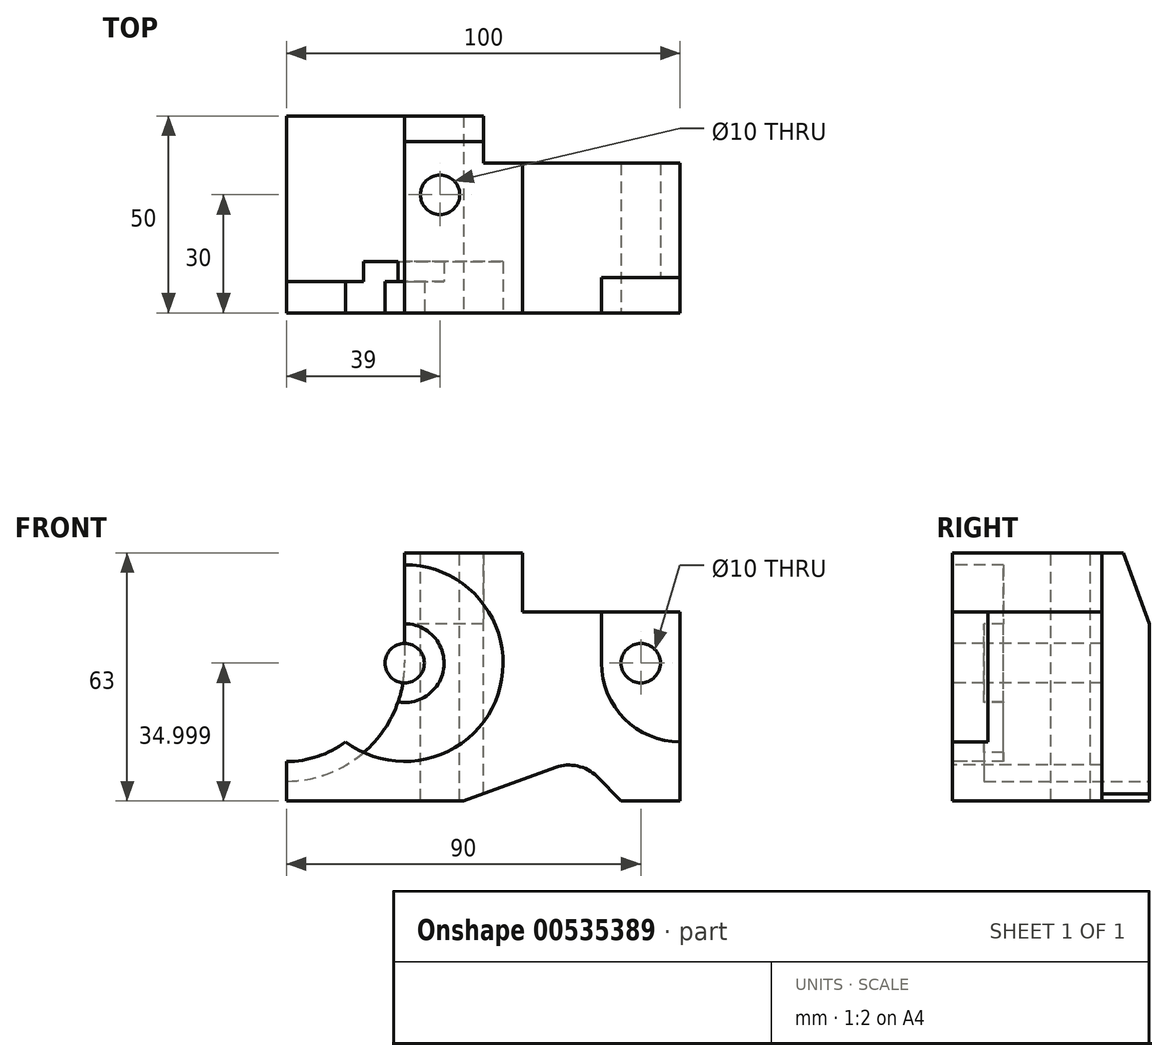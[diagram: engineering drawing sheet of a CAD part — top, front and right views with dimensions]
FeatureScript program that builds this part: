
annotation { "Feature Type Name" : "Feature", "Feature Type Description" : "" }
export const myFeature = defineFeature(function(context is Context, id is Id, definition is map)
    precondition{}
    {
        {
            var Q0;
            Q0=qCreatedBy(makeId("Front.planeOp"),FACE);
            var sketch = newSketch(context, id + "F0", { "sketchPlane" : qUnion([Q0])});
            skLineSegment(sketch, "E0.bottom", {"start": v(-90, 41.77) * mm, "end": v(-30, 41.77) * mm});
            skLineSegment(sketch, "E0.top", {"start": v(-90, -21.23) * mm, "end": v(-45, -21.23) * mm});
            skLineSegment(sketch, "E0.left", {"start": v(-90, 41.77) * mm, "end": v(-90, 38.77) * mm});
            skLineSegment(sketch, "E0.right", {"start": v(10, 26.77) * mm, "end": v(10, -21.23) * mm});
            skLineSegment(sketch, "E1", {"start": v(-45, -21.23) * mm, "end": v(-21.66, -12.74) * mm});
            skLineSegment(sketch, "E2", {"start": v(-11.17, -15.06) * mm, "end": v(-5, -21.23) * mm});
            skPoint(sketch, "E3.visualSharp", {"position": v(-15.67, -10.56) * mm});
            skArc(sketch, "E3.filletArc", {"start": v(-11.17, -15.06) * mm, "mid": v(-16.08, -12.37) * mm, "end": v(-21.66, -12.74) * mm});
            skLineSegment(sketch, "E4.trimOffspring", {"start": v(-5, -21.23) * mm, "end": v(10, -21.23) * mm});
            skLineSegment(sketch, "E5.top", {"start": v(-30, 26.77) * mm, "end": v(10, 26.77) * mm});
            skLineSegment(sketch, "E5.left", {"start": v(-30, 41.77) * mm, "end": v(-30, 26.77) * mm});
            skCircle(sketch, "E6", {"center": v(0, 13.77) * mm, "radius": 5 * mm});
            skArc(sketch, "E7", {"start": v(-90, -11.23) * mm, "mid": v(-65, 13.77) * mm, "end": v(-90, 38.77) * mm});
            skLineSegment(sketch, "E8", {"start": v(-65, 13.47) * mm, "end": v(-65, 14.07) * mm});
            skLineSegment(sketch, "E9.trimOffspring", {"start": v(-90, -11.23) * mm, "end": v(-90, -21.23) * mm});
            skSolve(sketch);
        }
        {
            var Q0;
            Q0 = qSketchRegion(id + "F0", true);
            extrude(context, id + "F1", {"entities" : qUnion([Q0]), "oppositeDirection" : true, "depth" : 50 * mm, "offsetDistance" : 25 * mm});
        }
        {
            var Q0;
            Q0=makeQuery(id+"F1.opExtrude","CAP_FACE",FACE,{"disambiguationData":[OSD([sQuery(id+"F0.wireOp",EDGE,"E0.bottom"),sQuery(id+"F0.wireOp",EDGE,"E0.top"),sQuery(id+"F0.wireOp",EDGE,"E0.left"),sQuery(id+"F0.wireOp",EDGE,"E0.right"),sQuery(id+"F0.wireOp",EDGE,"E1"),sQuery(id+"F0.wireOp",EDGE,"E2"),sQuery(id+"F0.wireOp",EDGE,"E3.filletArc"),sQuery(id+"F0.wireOp",EDGE,"E4.trimOffspring"),sQuery(id+"F0.wireOp",EDGE,"E5.top"),sQuery(id+"F0.wireOp",EDGE,"E5.left"),sQuery(id+"F0.wireOp",EDGE,"E6"),sQuery(id+"F0.wireOp",EDGE,"E7"),sQuery(id+"F0.wireOp",EDGE,"E8"),sQuery(id+"F0.wireOp",EDGE,"E9.trimOffspring")])],"isStart":false});
            var sketch = newSketch(context, id + "F2", { "sketchPlane" : qUnion([Q0])});
            skArc(sketch, "E10", {"start": v(60, 13.77) * mm, "mid": v(111.21, -7.44) * mm, "end": v(90, 43.77) * mm});
            skLineSegment(sketch, "E11", {"start": v(60, 43.77) * mm, "end": v(60, 13.77) * mm});
            skLineSegment(sketch, "E12", {"start": v(60, 43.77) * mm, "end": v(90, 43.77) * mm});
            skSolve(sketch);
        }
        {
            var Q0;
            Q0 = qSketchRegion(id + "F2", true);
            extrude(context, id + "F3", {"entities" : qUnion([Q0]), "operationType" : NewBodyOperationType.REMOVE, "oppositeDirection" : true, "depth" : 42 * mm, "offsetDistance" : 25 * mm});
        }
        {
            var Q0;
            Q0=makeQuery(id+"F3.boolean.opBoolean","COPY",FACE,{"derivedFrom":makeQuery(id+"F3.opExtrude","SWEPT_FACE",FACE,{"disambiguationData":[OSD([sQuery(id+"F2.wireOp",EDGE,"E11")])]})});
            var sketch = newSketch(context, id + "F4", { "sketchPlane" : qUnion([Q0])});
            skLineSegment(sketch, "E13", {"start": v(-50, 23.77) * mm, "end": v(-43.45, 41.77) * mm});
            skLineSegment(sketch, "E14", {"start": v(-43.45, 41.77) * mm, "end": v(-50, 41.77) * mm});
            skLineSegment(sketch, "E15", {"start": v(-50, 41.77) * mm, "end": v(-50, 23.77) * mm});
            skSolve(sketch);
        }
        {
            var Q0;
            Q0 = qSketchRegion(id + "F4", true);
            extrude(context, id + "F5", {"entities" : qUnion([Q0]), "operationType" : NewBodyOperationType.REMOVE, "endBound" : BoundingType.THROUGH_ALL, "oppositeDirection" : true, "depth" : 25 * mm, "offsetDistance" : 25 * mm});
        }
        {
            var Q0;
            Q0=makeQuery(id+"F1.opExtrude","CAP_FACE",FACE,{"disambiguationData":[OSD([sQuery(id+"F0.wireOp",EDGE,"E0.bottom"),sQuery(id+"F0.wireOp",EDGE,"E0.top"),sQuery(id+"F0.wireOp",EDGE,"E0.left"),sQuery(id+"F0.wireOp",EDGE,"E0.right"),sQuery(id+"F0.wireOp",EDGE,"E1"),sQuery(id+"F0.wireOp",EDGE,"E2"),sQuery(id+"F0.wireOp",EDGE,"E3.filletArc"),sQuery(id+"F0.wireOp",EDGE,"E4.trimOffspring"),sQuery(id+"F0.wireOp",EDGE,"E5.top"),sQuery(id+"F0.wireOp",EDGE,"E5.left"),sQuery(id+"F0.wireOp",EDGE,"E6"),sQuery(id+"F0.wireOp",EDGE,"E7"),sQuery(id+"F0.wireOp",EDGE,"E8"),sQuery(id+"F0.wireOp",EDGE,"E9.trimOffspring")])],"isStart":true});
            var sketch = newSketch(context, id + "F6", { "sketchPlane" : qUnion([Q0])});
            skArc(sketch, "E16", {"start": v(-85, 13.77) * mm, "mid": v(-42.32, -3.9) * mm, "end": v(-60, 38.77) * mm});
            skCircle(sketch, "E17", {"center": v(-60, 13.77) * mm, "radius": 10 * mm});
            skLineSegment(sketch, "E18", {"start": v(-60, 13.77) * mm, "end": v(-60, 23.77) * mm});
            skPoint(sketch, "E18.endSnap0", {"position": v(-60, 41.77) * mm});
            skLineSegment(sketch, "E19", {"start": v(-60, 47.56) * mm, "end": v(-93.34, 47.56) * mm});
            skLineSegment(sketch, "E20", {"start": v(-93.34, 47.56) * mm, "end": v(-93.34, 13.77) * mm});
            skLineSegment(sketch, "E21.trimOffspring", {"start": v(-60, 38.77) * mm, "end": v(-60, 47.56) * mm});
            skLineSegment(sketch, "E22", {"start": v(-93.34, 13.77) * mm, "end": v(-85, 13.77) * mm});
            skSolve(sketch);
        }
        {
            var Q0;
            Q0 = qSketchRegion(id + "F6", true);
            extrude(context, id + "F7", {"entities" : qUnion([Q0]), "operationType" : NewBodyOperationType.REMOVE, "oppositeDirection" : true, "depth" : 13 * mm, "offsetDistance" : 25 * mm});
        }
        {
            var Q0;
            {var subQ0=sQuery(id+"F0.wireOp",EDGE,"E9.trimOffspring");var subQ1=sQuery(id+"F0.wireOp",EDGE,"E7");var subQ2=sQuery(id+"F0.wireOp",EDGE,"E8");var subQ3=sQuery(id+"F0.wireOp",EDGE,"E0.left");Q0=makeQuery(id+"F7.boolean.opBoolean","SPLIT",FACE,{"disambiguationData":[TD([makeQuery(id+"F1.opExtrude","SWEPT_FACE",FACE,{"disambiguationData":[OSD([subQ2])]})])],"derivedFrom":makeQuery(id+"F1.opExtrude","CAP_FACE",FACE,{"disambiguationData":[OSD([sQuery(id+"F0.wireOp",EDGE,"E0.bottom"),sQuery(id+"F0.wireOp",EDGE,"E0.top"),subQ3,sQuery(id+"F0.wireOp",EDGE,"E0.right"),sQuery(id+"F0.wireOp",EDGE,"E1"),sQuery(id+"F0.wireOp",EDGE,"E2"),sQuery(id+"F0.wireOp",EDGE,"E3.filletArc"),sQuery(id+"F0.wireOp",EDGE,"E4.trimOffspring"),sQuery(id+"F0.wireOp",EDGE,"E5.top"),sQuery(id+"F0.wireOp",EDGE,"E5.left"),sQuery(id+"F0.wireOp",EDGE,"E6"),subQ1,subQ2,subQ0])],"isStart":true})});}
            var sketch = newSketch(context, id + "F8", { "sketchPlane" : qUnion([Q0])});
            skCircle(sketch, "E23", {"center": v(-60, 13.77) * mm, "radius": 5 * mm});
            skCircle(sketch, "E24", {"center": v(-60, 13.77) * mm, "radius": 11.33 * mm});
            skSolve(sketch);
        }
        {
            var Q0;
            Q0 = qSketchRegion(id + "F8", true);
            extrude(context, id + "F9", {"entities" : qUnion([Q0]), "operationType" : NewBodyOperationType.REMOVE, "oppositeDirection" : true, "depth" : 8 * mm, "offsetDistance" : 25 * mm});
        }
        {
            var Q0;
            Q0=makeQuery(id+"F1.opExtrude","SWEPT_FACE",FACE,{"disambiguationData":[OSD([sQuery(id+"F0.wireOp",EDGE,"E0.bottom")])]});
            var sketch = newSketch(context, id + "F10", { "sketchPlane" : qUnion([Q0])});
            skLineSegment(sketch, "E25.bottom", {"start": v(-40, 50) * mm, "end": v(10, 50) * mm});
            skLineSegment(sketch, "E25.top", {"start": v(-40, 38) * mm, "end": v(10, 38) * mm});
            skLineSegment(sketch, "E25.left", {"start": v(-40, 50) * mm, "end": v(-40, 38) * mm});
            skLineSegment(sketch, "E25.right", {"start": v(10, 50) * mm, "end": v(10, 38) * mm});
            skCircle(sketch, "E26", {"center": v(-51, 30) * mm, "radius": 5 * mm});
            skSolve(sketch);
        }
        {
            var Q0;
            {var subQ0=sQuery(id+"F10.wireOp",EDGE,"E25.left");var subQ1=sQuery(id+"F10.wireOp",EDGE,"E25.top");var subQ2=makeQuery(id+"F10.imprint","INTERSECT",VERTEX,{"derivedFrom":[subQ1,subQ0]});Q0=makeQuery(id+"F10.imprint","IMPRINT",FACE,{"disambiguationData":[TD([[makeQuery(id+"F10.imprint","IMPRINT",EDGE,{"disambiguationData":[TD([[subQ2,-1.0]])],"derivedFrom":subQ1}),1.0]])]});}
            var Q1;
            {var subQ1=sQuery(id+"F10.wireOp",EDGE,"E25.bottom");Q1=makeQuery(id+"F10.imprint","IMPRINT",FACE,{"disambiguationData":[TD([[makeQuery(id+"F10.imprint","IMPRINT",EDGE,{"derivedFrom":subQ1}),-1.0]])]});}
            var Q2;
            Q2=makeQuery(id+"F10.imprint","IMPRINT",FACE,{"disambiguationData":[TD([[makeQuery(id+"F10.imprint","IMPRINT",EDGE,{"derivedFrom":sQuery(id+"F10.wireOp",EDGE,"E26")}),1.0]])]});
            extrude(context, id + "F11", {"entities" : qUnion([Q0, Q1, Q2]), "operationType" : NewBodyOperationType.REMOVE, "endBound" : BoundingType.THROUGH_ALL, "oppositeDirection" : true, "depth" : 25 * mm, "offsetDistance" : 25 * mm});
        }
        {
            var Q0;
            {var subQ0=sQuery(id+"F0.wireOp",EDGE,"E6");var subQ1=sQuery(id+"F0.wireOp",EDGE,"E5.top");var subQ2=sQuery(id+"F0.wireOp",EDGE,"E4.trimOffspring");var subQ3=sQuery(id+"F0.wireOp",EDGE,"E3.filletArc");var subQ4=sQuery(id+"F0.wireOp",EDGE,"E2");var subQ5=sQuery(id+"F0.wireOp",EDGE,"E5.left");var subQ6=sQuery(id+"F0.wireOp",EDGE,"E0.bottom");var subQ7=sQuery(id+"F0.wireOp",EDGE,"E0.right");var subQ8=sQuery(id+"F0.wireOp",EDGE,"E0.top");var subQ9=sQuery(id+"F0.wireOp",EDGE,"E1");var subQ10=sQuery(id+"F0.wireOp",EDGE,"E9.trimOffspring");var subQ11=sQuery(id+"F0.wireOp",EDGE,"E7");var subQ12=sQuery(id+"F0.wireOp",EDGE,"E8");Q0=makeQuery(id+"F7.boolean.opBoolean","SPLIT",FACE,{"disambiguationData":[TD([makeQuery(id+"F1.opExtrude","SWEPT_FACE",FACE,{"disambiguationData":[OSD([subQ6])]})])],"derivedFrom":makeQuery(id+"F1.opExtrude","CAP_FACE",FACE,{"disambiguationData":[OSD([subQ6,subQ8,sQuery(id+"F0.wireOp",EDGE,"E0.left"),subQ7,subQ9,subQ4,subQ3,subQ2,subQ1,subQ5,subQ0,subQ11,subQ12,subQ10])],"isStart":true})});}
            var sketch = newSketch(context, id + "F12", { "sketchPlane" : qUnion([Q0])});
            skLineSegment(sketch, "E27.bottom", {"start": v(-5.2, 26.77) * mm, "end": v(-10, 26.77) * mm});
            skLineSegment(sketch, "E27.right", {"start": v(-10, 26.77) * mm, "end": v(-10, 13.77) * mm});
            skArc(sketch, "E28", {"start": v(-10, 13.77) * mm, "mid": v(28.76, 6.84) * mm, "end": v(-5.2, 26.77) * mm});
            skSolve(sketch);
        }
        {
            var Q0;
            Q0 = qSketchRegion(id + "F12", true);
            extrude(context, id + "F13", {"entities" : qUnion([Q0]), "operationType" : NewBodyOperationType.REMOVE, "oppositeDirection" : true, "depth" : 9 * mm, "offsetDistance" : 25 * mm});
        }
    });
